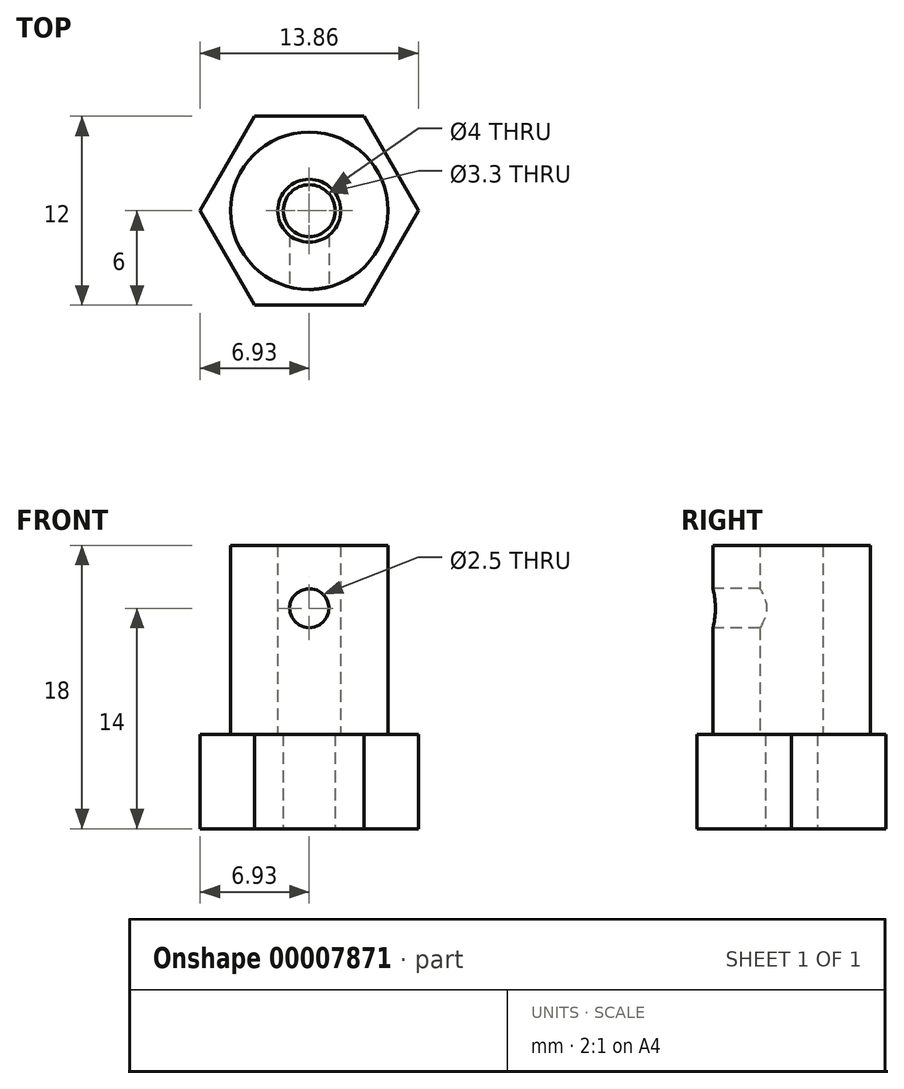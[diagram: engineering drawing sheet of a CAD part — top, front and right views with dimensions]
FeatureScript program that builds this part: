
annotation { "Feature Type Name" : "Feature", "Feature Type Description" : "" }
export const myFeature = defineFeature(function(context is Context, id is Id, definition is map)
    precondition{}
    {
        {
            var Q0;
            Q0=qCreatedBy(makeId("Top.planeOp"),FACE);
            var sketch = newSketch(context, id + "F0", { "sketchPlane" : qUnion([Q0])});
            skCircle(sketch, "E0.cCircle", {"center": v(0, 0) * mm, "radius": 6 * mm, "construction": true});
            skLineSegment(sketch, "E0.0", {"start": v(-3.46, 6) * mm, "end": v(3.46, 6) * mm});
            skLineSegment(sketch, "E0.1", {"start": v(3.46, 6) * mm, "end": v(6.93, 0) * mm});
            skLineSegment(sketch, "E0.2", {"start": v(6.93, 0) * mm, "end": v(3.46, -6) * mm});
            skLineSegment(sketch, "E0.3", {"start": v(3.46, -6) * mm, "end": v(-3.46, -6) * mm});
            skLineSegment(sketch, "E0.4", {"start": v(-3.46, -6) * mm, "end": v(-6.93, 0) * mm});
            skLineSegment(sketch, "E0.5", {"start": v(-6.93, 0) * mm, "end": v(-3.46, 6) * mm});
            skPoint(sketch, "E0.0.midPoint", {"position": v(0, 6) * mm});
            skCircle(sketch, "E1", {"center": v(0, 0) * mm, "radius": 1.65 * mm});
            skSolve(sketch);
        }
        {
            var Q0;
            Q0=makeQuery(id+"F0.imprint","IMPRINT",FACE,{"disambiguationData":[TD([[makeQuery(id+"F0.imprint","IMPRINT",EDGE,{"derivedFrom":sQuery(id+"F0.wireOp",EDGE,"E0.0")}),-1.0]])]});
            extrude(context, id + "F1", {"entities" : qUnion([Q0]), "depth" : 6 * mm});
        }
        {
            var Q0;
            Q0=makeQuery(id+"F1.opExtrude","CAP_FACE",FACE,{"disambiguationData":[OSD([sQuery(id+"F0.wireOp",EDGE,"E0.0"),sQuery(id+"F0.wireOp",EDGE,"E0.1"),sQuery(id+"F0.wireOp",EDGE,"E0.2"),sQuery(id+"F0.wireOp",EDGE,"E0.3"),sQuery(id+"F0.wireOp",EDGE,"E0.4"),sQuery(id+"F0.wireOp",EDGE,"E0.5"),sQuery(id+"F0.wireOp",EDGE,"E1")])],"isStart":false});
            var sketch = newSketch(context, id + "F2", { "sketchPlane" : qUnion([Q0])});
            skCircle(sketch, "E2", {"center": v(0, 0) * mm, "radius": 5 * mm});
            skCircle(sketch, "E3", {"center": v(0, 0) * mm, "radius": 2 * mm});
            skSolve(sketch);
        }
        {
            var Q0;
            Q0=makeQuery(id+"F2.imprint","IMPRINT",FACE,{"disambiguationData":[TD([[makeQuery(id+"F2.imprint","IMPRINT",EDGE,{"derivedFrom":sQuery(id+"F2.wireOp",EDGE,"E2")}),1.0]])]});
            extrude(context, id + "F3", {"entities" : qUnion([Q0]), "depth" : 12 * mm});
        }
        {
            var Q0;
            Q0=makeQuery(id+"F1.opExtrude","SWEPT_FACE",FACE,{"disambiguationData":[OSD([sQuery(id+"F0.wireOp",EDGE,"E0.3")])]});
            var sketch = newSketch(context, id + "F4", { "sketchPlane" : qUnion([Q0])});
            skCircle(sketch, "E4", {"center": v(0, 14) * mm, "radius": 1.25 * mm});
            skSolve(sketch);
        }
        {
            var Q0;
            Q0=makeQuery(id+"F4.imprint","IMPRINT",FACE,{"disambiguationData":[TD([[makeQuery(id+"F4.imprint","IMPRINT",EDGE,{"derivedFrom":sQuery(id+"F4.wireOp",EDGE,"E4")}),1.0]])]});
            extrude(context, id + "F5", {"entities" : qUnion([Q0]), "operationType" : NewBodyOperationType.REMOVE, "oppositeDirection" : true, "depth" : 6 * mm});
        }
    });
